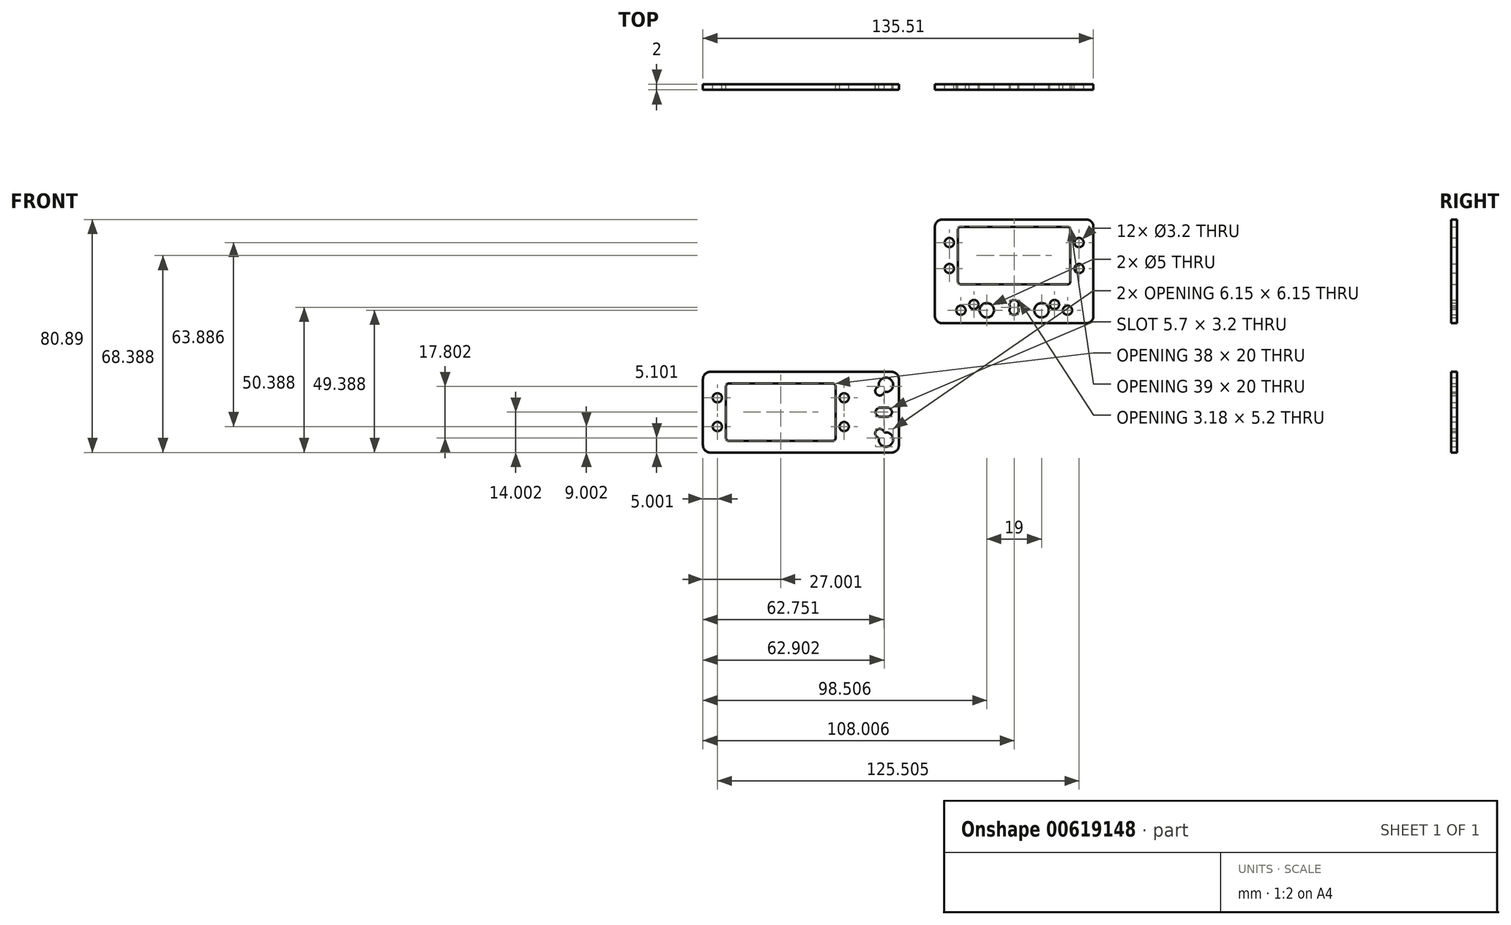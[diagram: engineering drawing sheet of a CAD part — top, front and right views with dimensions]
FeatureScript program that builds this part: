
annotation { "Feature Type Name" : "Feature", "Feature Type Description" : "" }
export const myFeature = defineFeature(function(context is Context, id is Id, definition is map)
    precondition{}
    {
        {
            var Q0;
            Q0=qCreatedBy(makeId("Front.planeOp"),FACE);
            var sketch = newSketch(context, id + "F0", { "sketchPlane" : qUnion([Q0])});
            skLineSegment(sketch, "E0.bottom", {"start": v(86.64, 87.29) * mm, "end": v(136.64, 87.29) * mm});
            skLineSegment(sketch, "E0.top", {"start": v(86.64, 51.29) * mm, "end": v(136.64, 51.29) * mm});
            skLineSegment(sketch, "E0.left", {"start": v(84.14, 84.79) * mm, "end": v(84.14, 53.79) * mm});
            skLineSegment(sketch, "E0.right", {"start": v(139.14, 84.79) * mm, "end": v(139.14, 53.79) * mm});
            skLineSegment(sketch, "E1.bottom", {"start": v(6.13, 34.4) * mm, "end": v(69.13, 34.4) * mm});
            skLineSegment(sketch, "E1.top", {"start": v(6.13, 6.4) * mm, "end": v(69.13, 6.4) * mm});
            skLineSegment(sketch, "E1.left", {"start": v(3.63, 31.9) * mm, "end": v(3.63, 8.9) * mm});
            skLineSegment(sketch, "E1.right", {"start": v(71.63, 31.9) * mm, "end": v(71.63, 8.9) * mm});
            skLineSegment(sketch, "E2", {"start": v(3.63, 20.4) * mm, "end": v(71.63, 20.4) * mm, "construction": true});
            skLineSegment(sketch, "E3.bottom", {"start": v(48.63, 30.4) * mm, "end": v(12.63, 30.4) * mm});
            skLineSegment(sketch, "E3.top", {"start": v(48.63, 10.4) * mm, "end": v(12.63, 10.4) * mm});
            skLineSegment(sketch, "E3.left", {"start": v(49.63, 29.4) * mm, "end": v(49.63, 11.4) * mm});
            skLineSegment(sketch, "E3.right", {"start": v(11.63, 29.4) * mm, "end": v(11.63, 11.4) * mm});
            skPoint(sketch, "E3.middle", {"position": v(30.63, 20.4) * mm});
            skLineSegment(sketch, "E4", {"start": v(71.63, 34.4) * mm, "end": v(57.63, 20.4) * mm, "construction": true});
            skPoint(sketch, "E5.visualSharp", {"position": v(3.63, 34.4) * mm});
            skArc(sketch, "E5.filletArc", {"start": v(6.13, 34.4) * mm, "mid": v(4.36, 33.67) * mm, "end": v(3.63, 31.9) * mm});
            skPoint(sketch, "E6.visualSharp", {"position": v(71.63, 34.4) * mm});
            skArc(sketch, "E6.filletArc", {"start": v(71.63, 31.9) * mm, "mid": v(70.9, 33.67) * mm, "end": v(69.13, 34.4) * mm});
            skPoint(sketch, "E7.visualSharp", {"position": v(71.63, 6.4) * mm});
            skArc(sketch, "E7.filletArc", {"start": v(69.13, 6.4) * mm, "mid": v(70.9, 7.13) * mm, "end": v(71.63, 8.9) * mm});
            skPoint(sketch, "E8.visualSharp", {"position": v(3.63, 6.4) * mm});
            skArc(sketch, "E8.filletArc", {"start": v(3.63, 8.9) * mm, "mid": v(4.36, 7.13) * mm, "end": v(6.13, 6.4) * mm});
            skPoint(sketch, "E9.visualSharp", {"position": v(11.63, 30.4) * mm});
            skArc(sketch, "E9.filletArc", {"start": v(12.63, 30.4) * mm, "mid": v(11.92, 30.1) * mm, "end": v(11.63, 29.4) * mm});
            skPoint(sketch, "E10.visualSharp", {"position": v(49.63, 30.4) * mm});
            skArc(sketch, "E10.filletArc", {"start": v(49.63, 29.4) * mm, "mid": v(49.34, 30.1) * mm, "end": v(48.63, 30.4) * mm});
            skPoint(sketch, "E11.visualSharp", {"position": v(49.63, 10.4) * mm});
            skArc(sketch, "E11.filletArc", {"start": v(48.63, 10.4) * mm, "mid": v(49.34, 10.7) * mm, "end": v(49.63, 11.4) * mm});
            skPoint(sketch, "E12.visualSharp", {"position": v(11.63, 10.4) * mm});
            skArc(sketch, "E12.filletArc", {"start": v(11.63, 11.4) * mm, "mid": v(11.92, 10.7) * mm, "end": v(12.63, 10.4) * mm});
            skCircle(sketch, "E13", {"center": v(8.63, 25.4) * mm, "radius": 1.6 * mm});
            skCircle(sketch, "E14", {"center": v(52.63, 25.4) * mm, "radius": 1.6 * mm});
            skCircle(sketch, "E15.MirrorC", {"center": v(8.63, 15.4) * mm, "radius": 1.6 * mm});
            skCircle(sketch, "E16.MirrorC", {"center": v(52.63, 15.4) * mm, "radius": 1.6 * mm});
            skArc(sketch, "E17", {"start": v(66.58, 27.46) * mm, "mid": v(68.9, 31.67) * mm, "end": v(64.7, 29.35) * mm});
            skArc(sketch, "E18", {"start": v(64.7, 29.35) * mm, "mid": v(63.88, 26.65) * mm, "end": v(66.58, 27.46) * mm});
            skArc(sketch, "E19.MirrorCS", {"start": v(64.7, 11.45) * mm, "mid": v(63.88, 14.15) * mm, "end": v(66.58, 13.34) * mm});
            skArc(sketch, "E20.MirrorCS", {"start": v(66.58, 13.34) * mm, "mid": v(68.9, 9.13) * mm, "end": v(64.7, 11.45) * mm});
            skArc(sketch, "E21", {"start": v(65.13, 22) * mm, "mid": v(63.53, 20.4) * mm, "end": v(65.13, 18.8) * mm});
            skArc(sketch, "E22", {"start": v(67.63, 18.8) * mm, "mid": v(69.23, 20.4) * mm, "end": v(67.63, 22) * mm});
            skLineSegment(sketch, "E23", {"start": v(65.13, 22) * mm, "end": v(67.63, 22) * mm});
            skLineSegment(sketch, "E24", {"start": v(65.13, 18.8) * mm, "end": v(67.63, 18.8) * mm});
            skLineSegment(sketch, "E25", {"start": v(84.14, 74.79) * mm, "end": v(139.14, 74.79) * mm, "construction": true});
            skLineSegment(sketch, "E26.bottom", {"start": v(130.14, 84.79) * mm, "end": v(93.14, 84.79) * mm});
            skLineSegment(sketch, "E26.top", {"start": v(130.14, 64.79) * mm, "end": v(93.14, 64.79) * mm});
            skLineSegment(sketch, "E26.left", {"start": v(131.14, 83.79) * mm, "end": v(131.14, 65.79) * mm});
            skLineSegment(sketch, "E26.right", {"start": v(92.14, 83.79) * mm, "end": v(92.14, 65.79) * mm});
            skPoint(sketch, "E26.middle", {"position": v(111.64, 74.79) * mm});
            skCircle(sketch, "E27", {"center": v(89.14, 79.29) * mm, "radius": 1.6 * mm});
            skCircle(sketch, "E28", {"center": v(134.14, 79.29) * mm, "radius": 1.6 * mm});
            skCircle(sketch, "E29.MirrorC", {"center": v(89.14, 70.29) * mm, "radius": 1.6 * mm});
            skCircle(sketch, "E30.MirrorC", {"center": v(134.14, 70.29) * mm, "radius": 1.6 * mm});
            skPoint(sketch, "E31.visualSharp", {"position": v(92.14, 84.79) * mm});
            skArc(sketch, "E31.filletArc", {"start": v(93.14, 84.79) * mm, "mid": v(92.43, 84.5) * mm, "end": v(92.14, 83.79) * mm});
            skPoint(sketch, "E32.visualSharp", {"position": v(131.14, 84.79) * mm});
            skArc(sketch, "E32.filletArc", {"start": v(131.14, 83.79) * mm, "mid": v(130.84, 84.5) * mm, "end": v(130.14, 84.79) * mm});
            skPoint(sketch, "E33.visualSharp", {"position": v(131.14, 64.79) * mm});
            skArc(sketch, "E33.filletArc", {"start": v(130.14, 64.79) * mm, "mid": v(130.84, 65.08) * mm, "end": v(131.14, 65.79) * mm});
            skPoint(sketch, "E34.visualSharp", {"position": v(92.14, 64.79) * mm});
            skArc(sketch, "E34.filletArc", {"start": v(92.14, 65.79) * mm, "mid": v(92.43, 65.08) * mm, "end": v(93.14, 64.79) * mm});
            skPoint(sketch, "E35.visualSharp", {"position": v(84.14, 87.29) * mm});
            skArc(sketch, "E35.filletArc", {"start": v(86.64, 87.29) * mm, "mid": v(84.87, 86.56) * mm, "end": v(84.14, 84.79) * mm});
            skPoint(sketch, "E36.visualSharp", {"position": v(139.14, 87.29) * mm});
            skArc(sketch, "E36.filletArc", {"start": v(139.14, 84.79) * mm, "mid": v(138.4, 86.56) * mm, "end": v(136.64, 87.29) * mm});
            skPoint(sketch, "E37.visualSharp", {"position": v(139.14, 51.29) * mm});
            skArc(sketch, "E37.filletArc", {"start": v(136.64, 51.29) * mm, "mid": v(138.4, 52.02) * mm, "end": v(139.14, 53.79) * mm});
            skPoint(sketch, "E38.visualSharp", {"position": v(84.14, 51.29) * mm});
            skArc(sketch, "E38.filletArc", {"start": v(84.14, 53.79) * mm, "mid": v(84.87, 52.02) * mm, "end": v(86.64, 51.29) * mm});
            skLineSegment(sketch, "E39", {"start": v(111.64, 74.79) * mm, "end": v(111.64, 51.29) * mm, "construction": true});
            skCircle(sketch, "E40", {"center": v(97.64, 57.79) * mm, "radius": 1.6 * mm});
            skCircle(sketch, "E41", {"center": v(93.14, 55.79) * mm, "radius": 1.6 * mm});
            skCircle(sketch, "E42", {"center": v(102.14, 55.79) * mm, "radius": 2.5 * mm});
            skArc(sketch, "E43", {"start": v(112.89, 56.79) * mm, "mid": v(111.64, 59.39) * mm, "end": v(110.39, 56.79) * mm});
            skArc(sketch, "E44", {"start": v(110.39, 56.79) * mm, "mid": v(111.64, 54.19) * mm, "end": v(112.89, 56.79) * mm});
            skCircle(sketch, "E45.MirrorC", {"center": v(121.14, 55.79) * mm, "radius": 2.5 * mm});
            skCircle(sketch, "E46.MirrorC", {"center": v(125.64, 57.79) * mm, "radius": 1.6 * mm});
            skCircle(sketch, "E47.MirrorC", {"center": v(130.14, 55.79) * mm, "radius": 1.6 * mm});
            skSolve(sketch);
        }
        {
            var Q0;
            Q0=makeQuery(id+"F0.imprint","IMPRINT",FACE,{"disambiguationData":[TD([[makeQuery(id+"F0.imprint","IMPRINT",EDGE,{"derivedFrom":sQuery(id+"F0.wireOp",EDGE,"E0.bottom")}),-1.0]])]});
            extrude(context, id + "F1", {"entities" : qUnion([Q0]), "depth" : 2 * mm, "offsetDistance" : 25 * mm});
        }
        {
            var Q0;
            Q0=makeQuery(id+"F0.imprint","IMPRINT",FACE,{"disambiguationData":[TD([[makeQuery(id+"F0.imprint","IMPRINT",EDGE,{"derivedFrom":sQuery(id+"F0.wireOp",EDGE,"E1.bottom")}),-1.0]])]});
            extrude(context, id + "F2", {"entities" : qUnion([Q0]), "depth" : 2 * mm, "offsetDistance" : 25 * mm});
        }
    });
